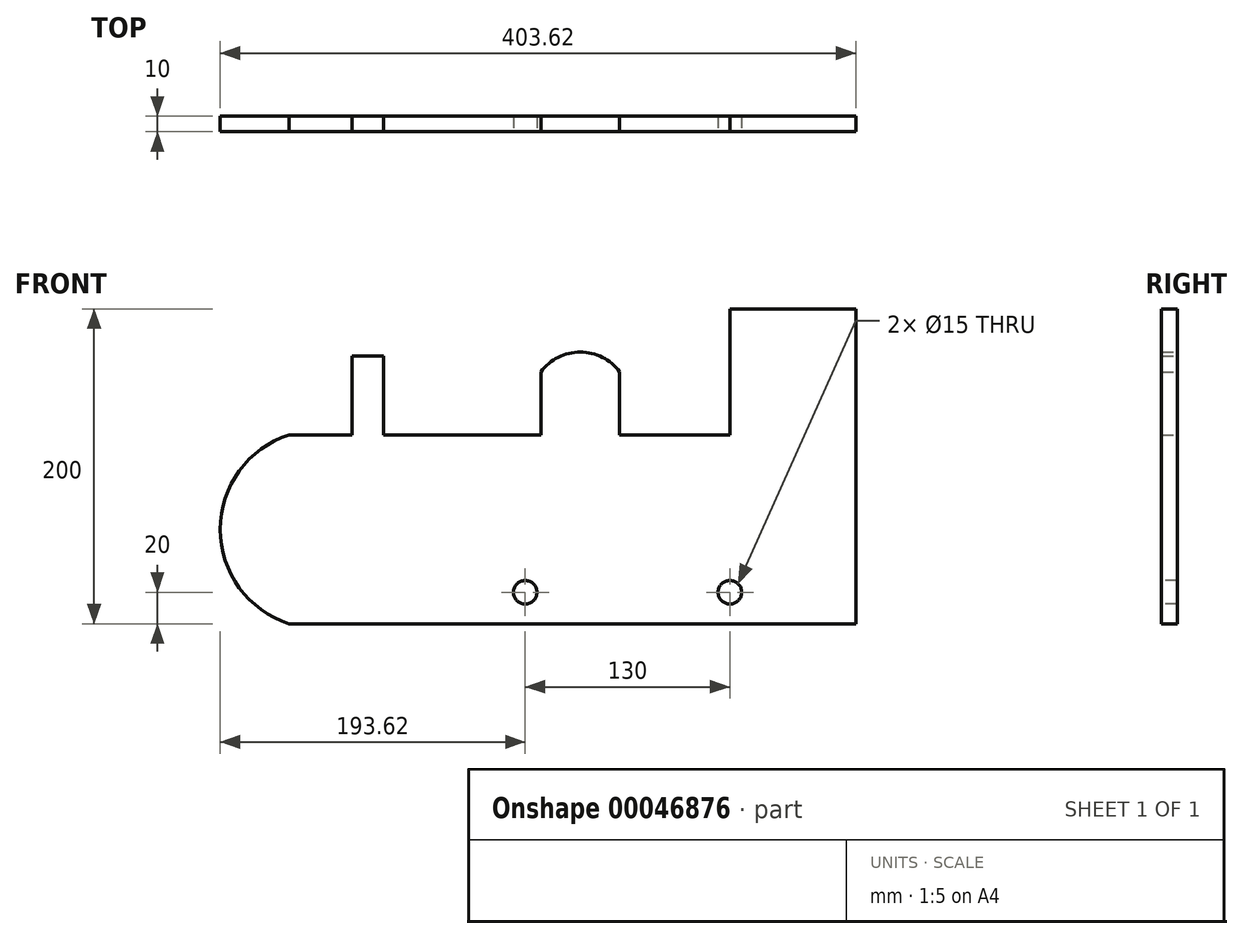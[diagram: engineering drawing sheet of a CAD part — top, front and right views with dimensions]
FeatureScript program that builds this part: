
annotation { "Feature Type Name" : "Feature", "Feature Type Description" : "" }
export const myFeature = defineFeature(function(context is Context, id is Id, definition is map)
    precondition{}
    {
        {
            var Q0;
            Q0=qCreatedBy(makeId("Front.planeOp"),FACE);
            var sketch = newSketch(context, id + "F0", { "sketchPlane" : qUnion([Q0])});
            skLineSegment(sketch, "E0.bottom", {"start": v(0, 0) * mm, "end": v(360, 0) * mm});
            skLineSegment(sketch, "E0.top", {"start": v(0, 120) * mm, "end": v(360, 120) * mm});
            skLineSegment(sketch, "E0.left", {"start": v(0, 0) * mm, "end": v(0, 120) * mm});
            skLineSegment(sketch, "E0.right", {"start": v(360, 0) * mm, "end": v(360, 120) * mm});
            skArc(sketch, "E1", {"start": v(0, 120) * mm, "mid": v(-43.62, 60) * mm, "end": v(0, 0) * mm});
            skLineSegment(sketch, "E2.bottom", {"start": v(40, 120) * mm, "end": v(60, 120) * mm});
            skLineSegment(sketch, "E2.top", {"start": v(40, 170) * mm, "end": v(60, 170) * mm});
            skLineSegment(sketch, "E2.left", {"start": v(40, 120) * mm, "end": v(40, 170) * mm});
            skLineSegment(sketch, "E2.right", {"start": v(60, 120) * mm, "end": v(60, 170) * mm});
            skLineSegment(sketch, "E3.bottom", {"start": v(160, 120) * mm, "end": v(210, 120) * mm});
            skLineSegment(sketch, "E3.top", {"start": v(160, 160) * mm, "end": v(210, 160) * mm});
            skLineSegment(sketch, "E3.left", {"start": v(160, 120) * mm, "end": v(160, 160) * mm});
            skLineSegment(sketch, "E3.right", {"start": v(210, 120) * mm, "end": v(210, 160) * mm});
            skArc(sketch, "E4", {"start": v(210, 160) * mm, "mid": v(185, 172.6) * mm, "end": v(160, 160) * mm});
            skLineSegment(sketch, "E5.bottom", {"start": v(360, 120) * mm, "end": v(280, 120) * mm});
            skLineSegment(sketch, "E5.top", {"start": v(360, 200) * mm, "end": v(280, 200) * mm});
            skLineSegment(sketch, "E5.left", {"start": v(360, 120) * mm, "end": v(360, 200) * mm});
            skLineSegment(sketch, "E5.right", {"start": v(280, 120) * mm, "end": v(280, 200) * mm});
            skPoint(sketch, "E6", {"position": v(185, 160) * mm});
            skSolve(sketch);
        }
        {
            var Q0;
            Q0 = qSketchRegion(id + "F0", true);
            extrude(context, id + "F1", {"entities" : qUnion([Q0]), "depth" : 10 * mm});
        }
        {
            var Q0;
            Q0=makeQuery(id+"F1.opExtrude","CAP_FACE",FACE,{"disambiguationData":[OSD([sQuery(id+"F0.wireOp",EDGE,"E0.bottom"),sQuery(id+"F0.wireOp",EDGE,"E0.top"),sQuery(id+"F0.wireOp",EDGE,"E0.right"),sQuery(id+"F0.wireOp",EDGE,"E1"),sQuery(id+"F0.wireOp",EDGE,"E2.top"),sQuery(id+"F0.wireOp",EDGE,"E2.left"),sQuery(id+"F0.wireOp",EDGE,"E2.right"),sQuery(id+"F0.wireOp",EDGE,"E3.left"),sQuery(id+"F0.wireOp",EDGE,"E3.right"),sQuery(id+"F0.wireOp",EDGE,"E4"),sQuery(id+"F0.wireOp",EDGE,"E5.top"),sQuery(id+"F0.wireOp",EDGE,"E5.left"),sQuery(id+"F0.wireOp",EDGE,"E5.right")])],"isStart":false});
            var sketch = newSketch(context, id + "F2", { "sketchPlane" : qUnion([Q0])});
            skCircle(sketch, "E7", {"center": v(150, 20) * mm, "radius": 7.5 * mm});
            skCircle(sketch, "E8", {"center": v(280, 20) * mm, "radius": 7.5 * mm});
            skLineSegment(sketch, "E9", {"start": v(150, 20) * mm, "end": v(150, 0) * mm, "construction": true});
            skLineSegment(sketch, "E10", {"start": v(280, 20) * mm, "end": v(280, 0) * mm, "construction": true});
            skSolve(sketch);
        }
        {
            var Q0;
            Q0 = qSketchRegion(id + "F2", true);
            extrude(context, id + "F3", {"entities" : qUnion([Q0]), "operationType" : NewBodyOperationType.REMOVE, "endBound" : BoundingType.THROUGH_ALL, "oppositeDirection" : true, "depth" : 25 * mm});
        }
    });
